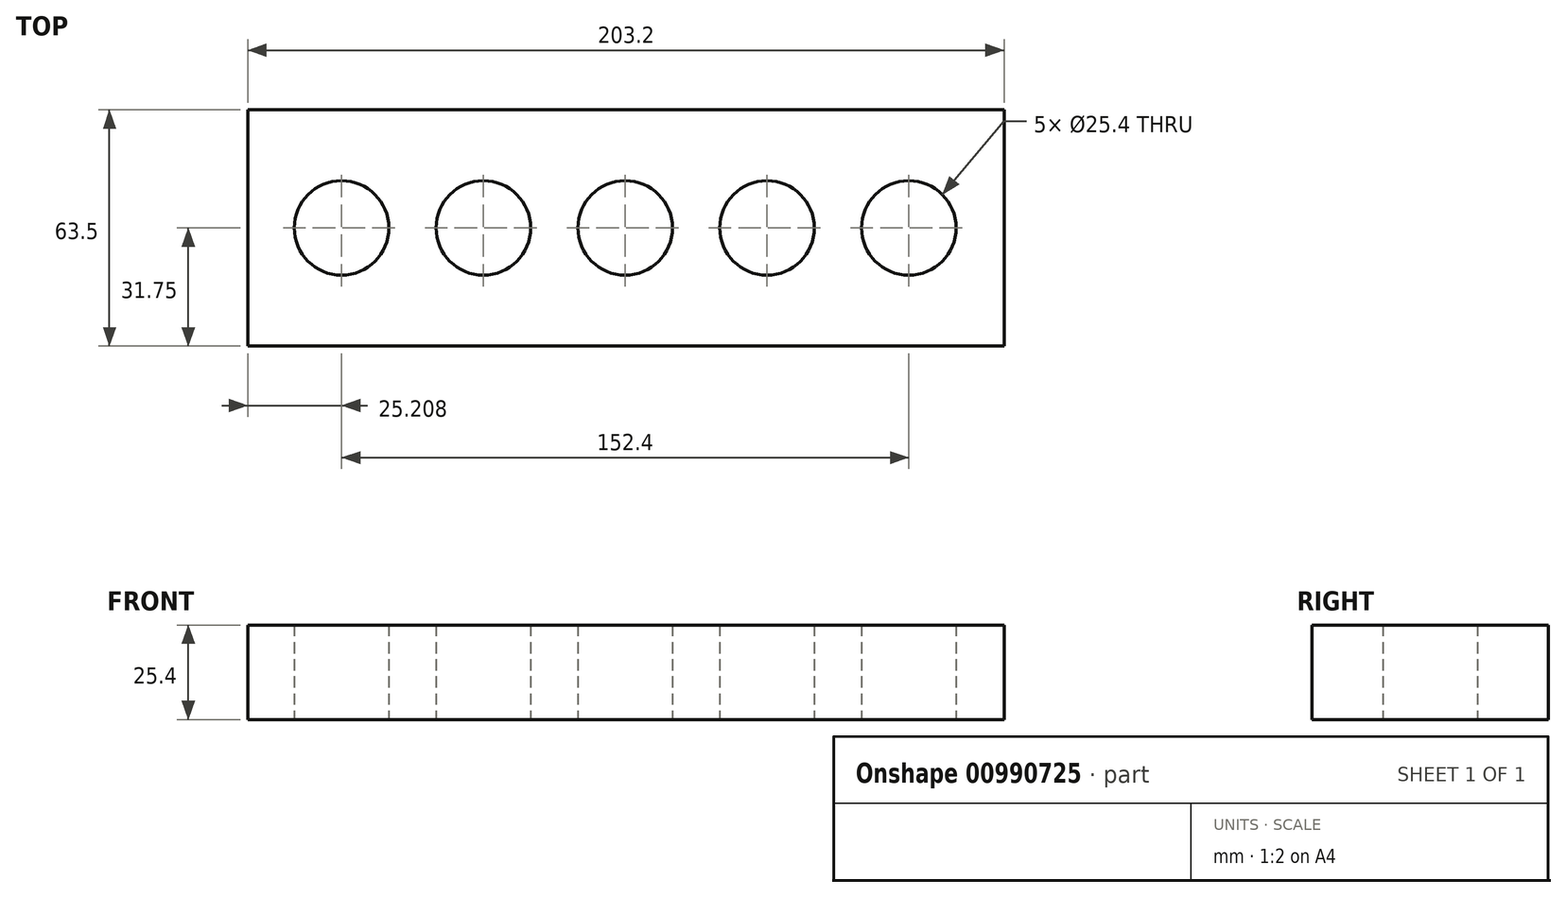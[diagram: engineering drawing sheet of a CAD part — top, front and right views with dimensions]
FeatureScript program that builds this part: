
annotation { "Feature Type Name" : "Feature", "Feature Type Description" : "" }
export const myFeature = defineFeature(function(context is Context, id is Id, definition is map)
    precondition{}
    {
        {
            var Q0;
            Q0=qCreatedBy(makeId("Top.planeOp"),FACE);
            var sketch = newSketch(context, id + "F0", { "sketchPlane" : qUnion([Q0])});
            skLineSegment(sketch, "E0.bottom", {"start": v(101.6, 31.75) * mm, "end": v(-101.6, 31.75) * mm});
            skLineSegment(sketch, "E0.top", {"start": v(101.6, -31.75) * mm, "end": v(-101.6, -31.75) * mm});
            skLineSegment(sketch, "E0.left", {"start": v(101.6, 31.75) * mm, "end": v(101.6, -31.75) * mm});
            skLineSegment(sketch, "E0.right", {"start": v(-101.6, 31.75) * mm, "end": v(-101.6, -31.75) * mm});
            skPoint(sketch, "E0.middle", {"position": v(0, 0) * mm});
            skLineSegment(sketch, "E1", {"start": v(0, 31.75) * mm, "end": v(-63.5, 31.75) * mm});
            skLineSegment(sketch, "E2", {"start": v(0, 31.75) * mm, "end": v(63.5, 31.75) * mm});
            skLineSegment(sketch, "E3.bottom", {"start": v(-63.5, 31.75) * mm, "end": v(63.5, 31.75) * mm});
            skLineSegment(sketch, "E3.top", {"start": v(-63.5, 31.75) * mm, "end": v(63.5, 31.75) * mm});
            skLineSegment(sketch, "E3.left", {"start": v(-63.5, 31.75) * mm, "end": v(-63.5, 31.75) * mm});
            skLineSegment(sketch, "E3.right", {"start": v(63.5, 31.75) * mm, "end": v(63.5, 31.75) * mm});
            skLineSegment(sketch, "E4", {"start": v(-63.5, 31.75) * mm, "end": v(-63.5, 95.25) * mm});
            skLineSegment(sketch, "E5", {"start": v(-63.5, 95.25) * mm, "end": v(63.5, 95.25) * mm});
            skLineSegment(sketch, "E6", {"start": v(63.5, 95.25) * mm, "end": v(63.5, 31.75) * mm});
            skCircle(sketch, "E7", {"center": v(-76.4, 0) * mm, "radius": 12.7 * mm});
            skCircle(sketch, "E8", {"center": v(-38.3, 0) * mm, "radius": 12.7 * mm});
            skCircle(sketch, "E9", {"center": v(-0.2, 0) * mm, "radius": 12.7 * mm});
            skCircle(sketch, "E10", {"center": v(37.9, 0) * mm, "radius": 12.7 * mm});
            skCircle(sketch, "E11", {"center": v(76, 0) * mm, "radius": 12.7 * mm});
            skSolve(sketch);
        }
        {
            var Q0;
            Q0=makeQuery(id+"F0.imprint","IMPRINT",FACE,{"disambiguationData":[TD([[makeQuery(id+"F0.imprint","IMPRINT",EDGE,{"derivedFrom":sQuery(id+"F0.wireOp",EDGE,"E0.top")}),-1.0]])]});
            var Q1;
            Q1=makeQuery(id+"F0.imprint","IMPRINT",FACE,{"disambiguationData":[TD([[makeQuery(id+"F0.imprint","IMPRINT",EDGE,{"derivedFrom":sQuery(id+"F0.wireOp",EDGE,"E3.top")}),1.0]])]});
            extrude(context, id + "F1", {"entities" : qUnion([Q0, Q1]), "depth" : 25.4 * mm, "offsetDistance" : 25.4 * mm});
        }
    });
